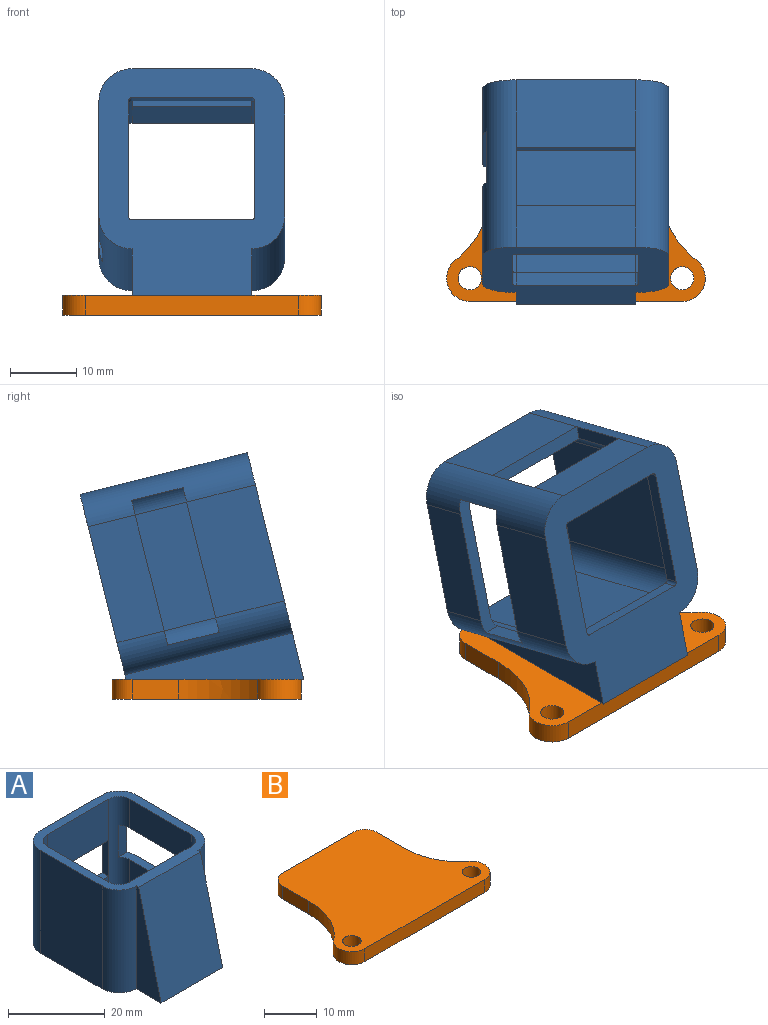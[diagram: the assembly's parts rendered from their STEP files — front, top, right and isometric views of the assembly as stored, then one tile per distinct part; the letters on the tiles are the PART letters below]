
ASSEMBLY  parts=2 mates=1
PART A: 41 faces, bbox 28x35.2x26 mm
  f0: plane 28.73x28mm, normal (0,0,1), area 207.3mm2, adj f2,f3,f4,f5,f6,f7,f11,f12
  f1: plane 35.22x28mm, normal (0,0,-1), area 531.6mm2, adj f3,f7,f8,f10,f12,f13,f14,f21
  f2: plane 18x7.32mm, normal (1,0,0), area 131.7mm2, adj f0,f3,f7,f35
  f3: cylinder r=5mm len=26mm, axis (0,0,-1), area 185.5mm2, adj f0,f1,f2,f8,f10,f11,f31,f34
  f4: cylinder r=3mm len=24mm, axis (0,0,-1), area 92.7mm2, adj f0,f5,f9,f15,f20,f29,f31,f34
  f5: plane 18x7.32mm, normal (-1,0,0), area 131.7mm2, adj f0,f4,f6,f35
  f6: cylinder r=3mm len=24mm, axis (0,0,-1), area 92.7mm2, adj f0,f5,f15,f16,f29,f35,f36,f37
  f7: cylinder r=5mm len=26mm, axis (0,0,-1), area 185.5mm2, adj f0,f1,f2,f10,f35,f36,f37,f38
  f8: plane 18x6.42mm, normal (0,1,0), area 115.6mm2, adj f1,f3,f12,f32
  f9: plane 18x4.42mm, normal (0,-1,0), area 79.6mm2, adj f4,f19,f29,f32
  f10: plane 18x10.68mm, normal (1,0,0), area 192.3mm2, adj f1,f3,f7,f37
  f11: plane 18x10.45mm, normal (0,1,0), area 188.2mm2, adj f0,f3,f12,f30
  f12: cylinder r=5mm len=26mm, axis (0,0,-1), area 204.2mm2, adj f0,f1,f8,f11,f13,f33
  f13: plane 26x18mm, normal (-1,0,0), area 468mm2, adj f0,f1,f12,f14
  f14: cylinder r=5mm len=26mm, axis (0,0,-1), area 204.2mm2, adj f0,f1,f13,f39
  f15: plane 18x8.68mm, normal (-1,0,0), area 156.3mm2, adj f4,f6,f29,f37
  f16: plane 24x18mm, normal (0,1,0), area 432mm2, adj f0,f6,f17,f29
  f17: cylinder r=3mm len=24mm, axis (0,0,-1), area 113.1mm2, adj f0,f16,f18,f29
  f18: plane 24x18mm, normal (1,0,0), area 432mm2, adj f0,f17,f19,f29
  f19: cylinder r=3mm len=24mm, axis (0,0,-1), area 113.1mm2, adj f0,f9,f18,f20,f29,f33
  f20: plane 18x10.45mm, normal (0,-1,0), area 188.2mm2, adj f0,f4,f19,f30
  f21: cylinder r=0.5mm len=2mm, axis (0,0,-1), area 1.6mm2, adj f1,f22,f28,f29
  f22: plane 18x2mm, normal (-1,0,0), area 36mm2, adj f1,f21,f23,f29
  f23: cylinder r=0.5mm len=2mm, axis (0,0,-1), area 1.6mm2, adj f1,f22,f24,f29
  f24: plane 18x2mm, normal (0,1,0), area 36mm2, adj f1,f23,f25,f29
  f25: cylinder r=0.5mm len=2mm, axis (0,0,-1), area 1.6mm2, adj f1,f24,f26,f29
  f26: plane 18x2mm, normal (1,0,0), area 36mm2, adj f1,f25,f27,f29
  f27: cylinder r=0.5mm len=2mm, axis (0,0,-1), area 1.6mm2, adj f1,f26,f28,f29
  f28: plane 18x2mm, normal (0,-1,0), area 36mm2, adj f1,f21,f27,f29
  f29: plane 24x24mm, normal (0,0,1), area 207.5mm2, adj f4,f6,f9,f15,f16,f17,f18,f19
  f30: plane 18x2mm, normal (0,0,-1), area 36mm2, adj f11,f20,f31,f33
  f31: plane 9.12x2mm, normal (-1,0,0), area 18.2mm2, adj f3,f4,f30,f32
  f32: plane 18x2mm, normal (0,0,1), area 36mm2, adj f8,f9,f31,f33
  f33: plane 9.12x2mm, normal (1,0,0), area 18.2mm2, adj f12,f19,f30,f32
  f34: plane 8x2.48mm, normal (0,-1,0), area 19.8mm2, adj f3,f4,f35,f37
  f35: plane 22.5x3.02mm, normal (0,0,-1), area 45.6mm2, adj f2,f3,f4,f5,f6,f7,f34,f36
  f36: plane 8x2.48mm, normal (0,1,0), area 19.8mm2, adj f6,f7,f35,f37
  f37: plane 22.5x3.02mm, normal (0,0,1), area 45.6mm2, adj f3,f4,f6,f7,f10,f15,f34,f36
  f38: plane 26x7.22mm, normal (1,0,0), area 103.2mm2, adj f0,f1,f7,f40
  f39: plane 26x7.22mm, normal (-1,0,0), area 103.2mm2, adj f0,f1,f14,f40
  f40: plane 26x18mm, normal (0,-0.97,0.24), area 482.4mm2, adj f0,f1,f38,f39
PART B: 14 faces, bbox 39x28.5x3 mm
  f0: plane 32.06x3mm, normal (0,-1,0), area 96.2mm2, adj f1,f11,f12,f13
  f1: cylinder r=3.5mm len=6.53mm, axis (0,0,-1), area 27.5mm2, adj f0,f2,f12,f13
  f2: extruded ~11.97x5.22mm, area 40.5mm2, adj f1,f3,f12,f13
  f3: plane 7x3mm, normal (1,0,0), area 21mm2, adj f2,f4,f12,f13
  f4: cylinder r=3mm len=3mm, axis (0,0,-1), area 14.1mm2, adj f3,f5,f12,f13
  f5: plane 19.04x3mm, normal (0,1,0), area 57.1mm2, adj f4,f6,f12,f13
  f6: cylinder r=3mm len=3mm, axis (0,0,-1), area 14.1mm2, adj f5,f7,f12,f13
  f7: plane 7x3mm, normal (-1,0,0), area 21mm2, adj f6,f8,f12,f13
  f8: extruded ~11.97x5.22mm, area 40.4mm2, adj f7,f11,f12,f13
  f9: cylinder r=1.75mm len=3.5mm, axis (0,0,-1), area 33mm2, adj f12,f13
  f10: cylinder r=1.75mm len=3.5mm, axis (0,0,-1), area 33mm2, adj f12,f13
  f11: cylinder r=3.5mm len=6.53mm, axis (0,0,-1), area 27.3mm2, adj f0,f8,f12,f13
  f12: plane 39x28.5mm, normal (0,0,1), area 810.2mm2, adj f0,f1,f2,f3,f4,f5,f6,f7
  f13: plane 39x28.5mm, normal (0,0,-1), area 810.2mm2, adj f0,f1,f2,f3,f4,f5,f6,f7
PLACE A rot(axis=(0,0.79,0.62),180deg) t=(0.06,-9.57,21.92)mm
PLACE B t=(0.09,4.2,-1.66)mm fixed
MATE planar A.f40 <-> B.f12  axis (0,0,-1) through (0.06,-1.3,1.34)mm
